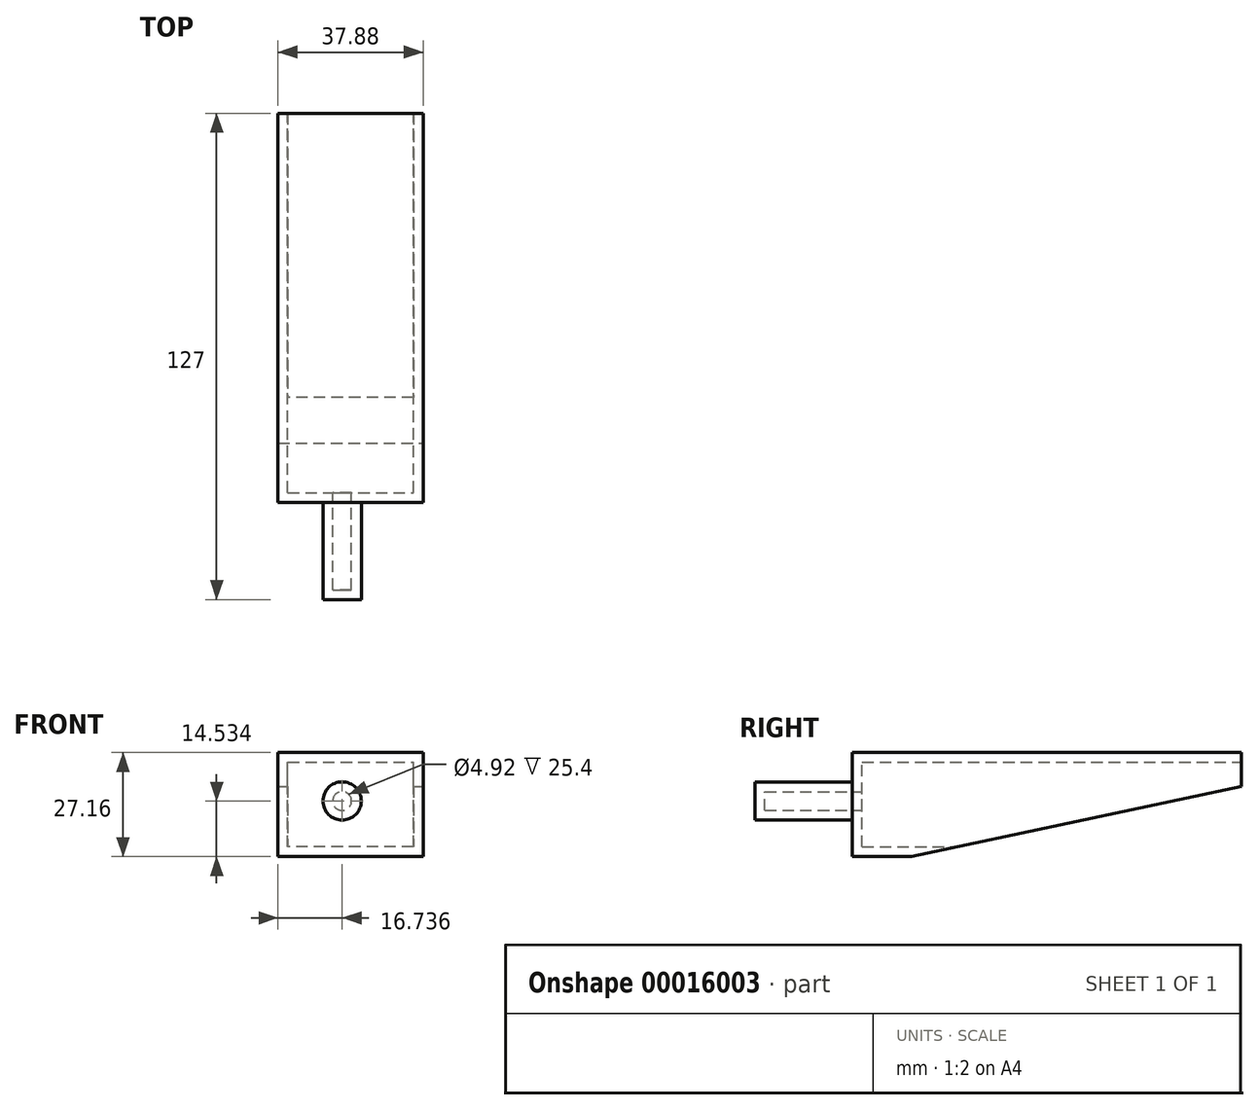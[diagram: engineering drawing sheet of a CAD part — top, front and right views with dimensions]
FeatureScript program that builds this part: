
annotation { "Feature Type Name" : "Feature", "Feature Type Description" : "" }
export const myFeature = defineFeature(function(context is Context, id is Id, definition is map)
    precondition{}
    {
        {
            var Q0;
            Q0=qCreatedBy(makeId("Front.planeOp"),FACE);
            var sketch = newSketch(context, id + "F0", { "sketchPlane" : qUnion([Q0])});
            skLineSegment(sketch, "E0.bottom", {"start": v(0, 0) * mm, "end": v(37.88, 0) * mm});
            skLineSegment(sketch, "E0.top", {"start": v(0, 27.16) * mm, "end": v(37.88, 27.16) * mm});
            skLineSegment(sketch, "E0.left", {"start": v(0, 0) * mm, "end": v(0, 27.16) * mm});
            skLineSegment(sketch, "E0.right", {"start": v(37.88, 0) * mm, "end": v(37.88, 27.16) * mm});
            skSolve(sketch);
        }
        {
            var Q0;
            Q0 = qSketchRegion(id + "F0", true);
            extrude(context, id + "F1", {"entities" : qUnion([Q0]), "depth" : 101.6 * mm});
        }
        {
            var Q0;
            Q0=makeQuery(id+"F1.opExtrude","CAP_FACE",FACE,{"disambiguationData":[OSD([sQuery(id+"F0.wireOp",EDGE,"E0.bottom"),sQuery(id+"F0.wireOp",EDGE,"E0.top"),sQuery(id+"F0.wireOp",EDGE,"E0.left"),sQuery(id+"F0.wireOp",EDGE,"E0.right")])],"isStart":false});
            var sketch = newSketch(context, id + "F2", { "sketchPlane" : qUnion([Q0])});
            skCircle(sketch, "E1", {"center": v(16.74, 14.53) * mm, "radius": 5 * mm});
            skSolve(sketch);
        }
        {
            var Q0;
            Q0 = qSketchRegion(id + "F2", true);
            extrude(context, id + "F3", {"entities" : qUnion([Q0]), "operationType" : NewBodyOperationType.ADD, "depth" : 25.4 * mm});
        }
        {
            var Q0;
            Q0=makeQuery(id+"F1.opExtrude","CAP_FACE",FACE,{"disambiguationData":[OSD([sQuery(id+"F0.wireOp",EDGE,"E0.bottom"),sQuery(id+"F0.wireOp",EDGE,"E0.top"),sQuery(id+"F0.wireOp",EDGE,"E0.left"),sQuery(id+"F0.wireOp",EDGE,"E0.right")])],"isStart":true});
            shell(context, id + "F4", {"entities" : qUnion([Q0]), "thickness" : 2.54 * mm});
        }
        {
            var Q0;
            Q0=makeQuery(id+"F1.opExtrude","SWEPT_FACE",FACE,{"disambiguationData":[OSD([sQuery(id+"F0.wireOp",EDGE,"E0.right")])]});
            var sketch = newSketch(context, id + "F5", { "sketchPlane" : qUnion([Q0])});
            skLineSegment(sketch, "E2", {"start": v(0, 17.18) * mm, "end": v(-85, 0) * mm});
            skLineSegment(sketch, "E3", {"start": v(0, 0) * mm, "end": v(0, 17.18) * mm});
            skSolve(sketch);
        }
        {
            var Q0;
            {var subQ1=sQuery(id+"F5.wireOp",EDGE,"E2");Q0=makeQuery(id+"F5.imprint","IMPRINT",FACE,{"disambiguationData":[TD([[makeQuery(id+"F5.imprint","IMPRINT",EDGE,{"derivedFrom":subQ1}),1.0]])]});}
            var sketch = newSketch(context, id + "F6", { "sketchPlane" : qUnion([Q0])});
            skLineSegment(sketch, "E4", {"start": v(0, 18.35) * mm, "end": v(0, 0) * mm});
            skLineSegment(sketch, "E5", {"start": v(0, 0) * mm, "end": v(-86.18, 0) * mm});
            skLineSegment(sketch, "E6", {"start": v(-86.18, 0) * mm, "end": v(0, 18.35) * mm});
            skSolve(sketch);
        }
        {
            var Q0;
            Q0 = qSketchRegion(id + "F6", true);
            extrude(context, id + "F7", {"entities" : qUnion([Q0]), "operationType" : NewBodyOperationType.REMOVE, "oppositeDirection" : true, "depth" : 101.6 * mm});
        }
    });
